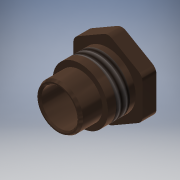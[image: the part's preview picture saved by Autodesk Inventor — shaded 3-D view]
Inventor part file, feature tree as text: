
AUTODESK INVENTOR PART (.ipt)
format: ipt  version: 2018 (Build 220112000, 112)  size: 196,096 bytes
history: native  units: mm (DEFAULTED — no unit token found)
features: chamfer x2, sketch x2, revolve x1, extrude x1, fillet x1, thread x1
ambient origin geometry x8: Origin, YZ Plane, XZ Plane, XY Plane, X Axis, Y Axis, Z Axis, Center Point
bodies: Solid1 (feature_tree)
feature tree (8):
  revolve  "Revolution1"  [1 undecoded]
  extrude  "Extrusion1"  Depth=8.0mm
  fillet  "Fillet1"  Radius=23.0mm
  chamfer  "Chamfer1"  Distance=2.0mm
  chamfer  "Chamfer2"  Distance=3.0mm
  thread  "Thread1"  [1 undecoded]
  sketch  "Sketch1"  dims[d0=13.0mm d1=16.0mm]
  sketch  "Sketch2"  dims[d2=20.0mm d3=8.0mm d4=23.0mm d5=2.0mm d6=3.0mm d7=2.0mm d8=90.0deg d9=25.0mm d10=5.0mm d11=0.0mm d12=3.0mm d13=0.5mm d14=2.0mm d15=0.5mm d16=1.0mm d17=5.0mm d18=3.0mm d19=45.0deg d20=45.0deg]
note: 2 required parameter values undecoded (feature->parameter linkage not recoverable at this tier; creation-order binding heuristic only, values carry confidence <= 0.55)